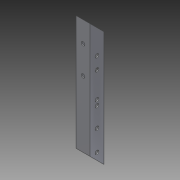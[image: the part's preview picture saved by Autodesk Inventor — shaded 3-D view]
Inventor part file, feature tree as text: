
AUTODESK INVENTOR PART (.ipt)
format: ipt  version: 2014 SP1 (Build 180222100, 222)  size: 128,512 bytes
history: native  units: in
note: dims shown in document units (in); Inventor stores cm internally (conversion verified against a paired STEP export)
features: reference x8, extrude x7, sketch x7
ambient origin geometry x8: Origin, YZ Plane, XZ Plane, XY Plane, X Axis, Y Axis, Z Axis, Center Point
bodies: Solid1 (feature_tree)
feature tree (22):
  extrude  "Extrusion1"  Depth=1.0in
  extrude  "Extrusion2"  Depth=0.0625in TaperAngle=0.0deg
  extrude  "Extrusion3"  Depth=1.0in TaperAngle=0.0deg
  extrude  "Extrusion4"  Depth=1.0in TaperAngle=0.0deg
  extrude  "Extrusion5"  Depth=1.0in
  extrude  "Extrusion6"  Depth=1.0in TaperAngle=0.0deg
  extrude  "Extrusion7"  Depth=1.0in
  sketch  "Sketch1"  dims[d0=1.0in d2=1.0in]
  sketch  "Sketch2"  dims[d3=0.0625in d4=10.0in d5=0.0in]
  sketch  "Sketch3"  dims[d6=1.0in d7=1.0in d8=0.0in]
  sketch  "Sketch4"  dims[d9=1.0in d10=0.0in d11=1.0in d12=0.0in]
  reference  "Reference1"
  reference  "Reference2"
  sketch  "Sketch5"  dims[d13=1.0in d14=0.75in]
  reference  "Reference3"
  reference  "Reference4"
  sketch  "Sketch6"  dims[d15=1.0in d16=0.0in d17=1.0in d18=0.0in]
  reference  "Reference5"
  reference  "Reference6"
  sketch  "Sketch7"  dims[d19=1.0in d20=0.0in d21=1.0in]
  reference  "Reference7"
  reference  "Reference8"
